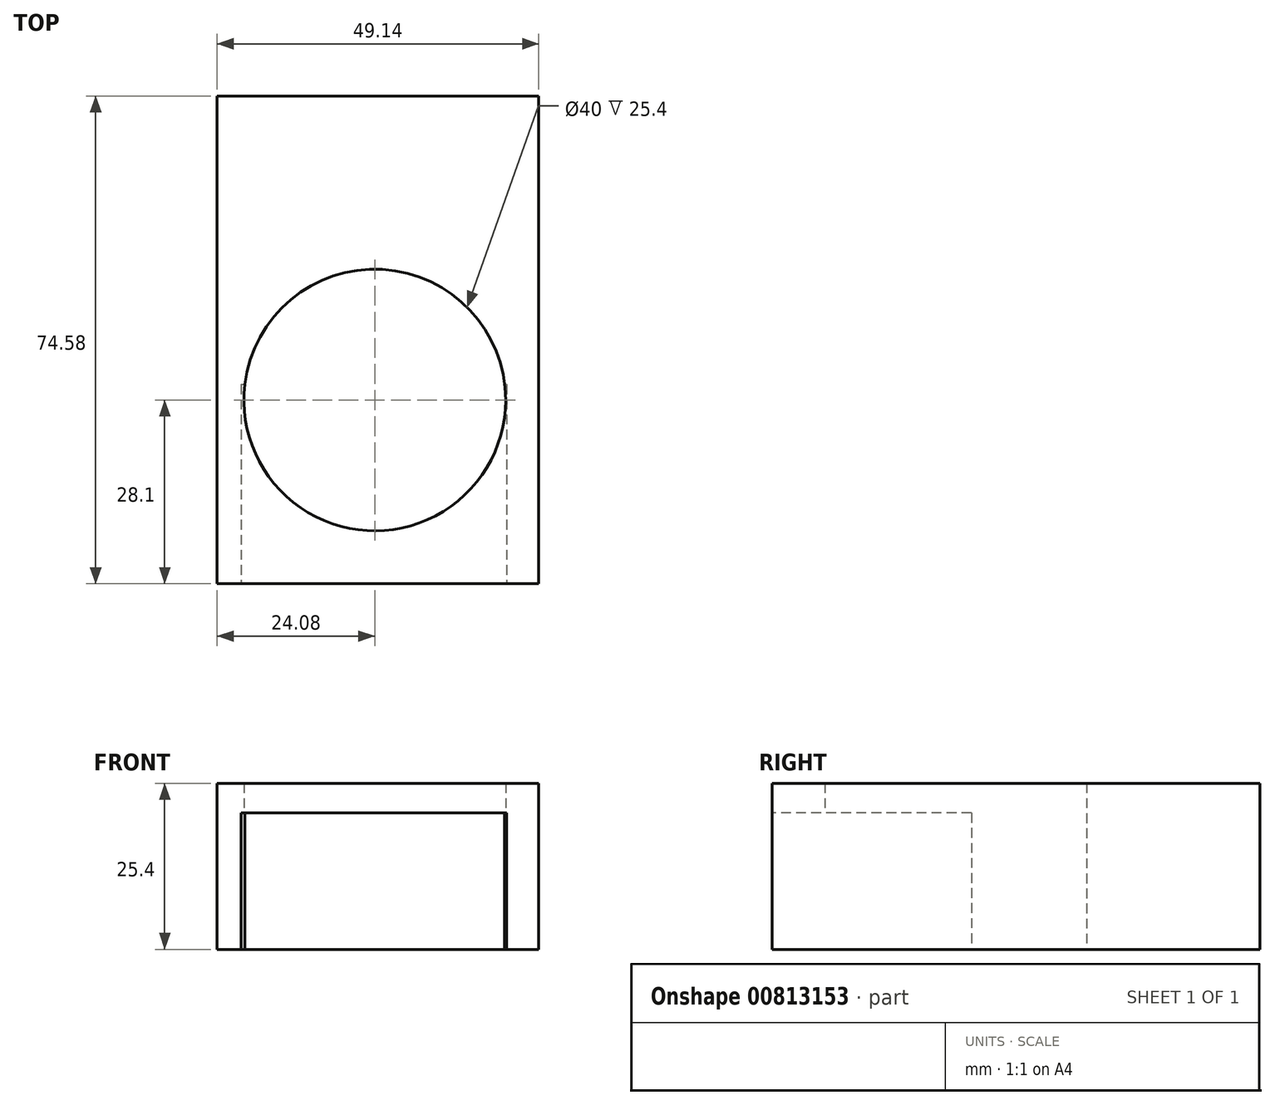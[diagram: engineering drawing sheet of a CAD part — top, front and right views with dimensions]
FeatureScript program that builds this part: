
annotation { "Feature Type Name" : "Feature", "Feature Type Description" : "" }
export const myFeature = defineFeature(function(context is Context, id is Id, definition is map)
    precondition{}
    {
        {
            var Q0;
            Q0=qCreatedBy(makeId("Top.planeOp"),FACE);
            var sketch = newSketch(context, id + "F0", { "sketchPlane" : qUnion([Q0])});
            skCircle(sketch, "E0", {"center": v(0, 0) * mm, "radius": 20 * mm});
            skSolve(sketch);
        }
        {
            var Q0;
            Q0=makeQuery(id+"F0.imprint","IMPRINT",FACE,{"disambiguationData":[TD([[makeQuery(id+"F0.imprint","IMPRINT",EDGE,{"derivedFrom":sQuery(id+"F0.wireOp",EDGE,"E0")}),1.0]])]});
            var sketch = newSketch(context, id + "F1", { "sketchPlane" : qUnion([Q0])});
            skLineSegment(sketch, "E1.bottom", {"start": v(-24.08, 46.48) * mm, "end": v(25.06, 46.48) * mm});
            skLineSegment(sketch, "E1.top", {"start": v(-24.08, -28.1) * mm, "end": v(25.06, -28.1) * mm});
            skLineSegment(sketch, "E1.left", {"start": v(-24.08, 46.48) * mm, "end": v(-24.08, -28.1) * mm});
            skLineSegment(sketch, "E1.right", {"start": v(25.06, 46.48) * mm, "end": v(25.06, -28.1) * mm});
            skSolve(sketch);
        }
        {
            var Q0;
            Q0=makeQuery(id+"F1.imprint","IMPRINT",FACE,{"disambiguationData":[TD([[makeQuery(id+"F1.imprint","IMPRINT",EDGE,{"derivedFrom":sQuery(id+"F1.wireOp",EDGE,"E1.bottom")}),-1.0]])]});
            extrude(context, id + "F2", {"entities" : qUnion([Q0]), "depth" : 25.4 * mm, "offsetDistance" : 25.4 * mm});
        }
        {
            var Q0;
            Q0=makeQuery(id+"F2.opExtrude","SWEPT_FACE",FACE,{"disambiguationData":[OSD([sQuery(id+"F1.wireOp",EDGE,"E1.top")])]});
            var sketch = newSketch(context, id + "F3", { "sketchPlane" : qUnion([Q0])});
            skLineSegment(sketch, "E2.bottom", {"start": v(-20.42, 20.86) * mm, "end": v(20.14, 20.86) * mm});
            skLineSegment(sketch, "E2.top", {"start": v(-20.42, 0) * mm, "end": v(20.14, 0) * mm});
            skLineSegment(sketch, "E2.left", {"start": v(-20.42, 20.86) * mm, "end": v(-20.42, 0) * mm});
            skLineSegment(sketch, "E2.right", {"start": v(20.14, 20.86) * mm, "end": v(20.14, 0) * mm});
            skSolve(sketch);
        }
        {
            var Q0;
            Q0=makeQuery(id+"F3.imprint","IMPRINT",FACE,{"disambiguationData":[TD([[makeQuery(id+"F3.imprint","IMPRINT",EDGE,{"derivedFrom":sQuery(id+"F3.wireOp",EDGE,"E2.bottom")}),-1.0]])]});
            extrude(context, id + "F4", {"entities" : qUnion([Q0]), "operationType" : NewBodyOperationType.REMOVE, "oppositeDirection" : true, "depth" : 30.48 * mm, "offsetDistance" : 25.4 * mm});
        }
    });
